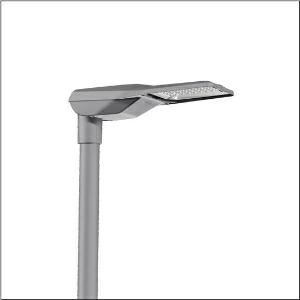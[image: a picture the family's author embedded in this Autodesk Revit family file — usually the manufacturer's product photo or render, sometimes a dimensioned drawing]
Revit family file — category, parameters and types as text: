
# Revit family: streetlight_sl_21_mini___st1_5a_5xe6p43a08hb_28db
name_source: partatom
category: Lighting Fixtures
units: mm (PartAtom-declared; Revit-internal decimal feet)

## family parameters
Cut with Voids When Loaded = No
Host = Face
Light Source = No
Part Type = Normal
Room Calculation Point = No
Round Connector Dimension = Use Diameter
Shared = No

## types (1)
- --- (1 x LED, 9260 lm, 66 W, 4000K)
    Apparent Load = 66 VA
    CIE Flux Codes = 22 53 95 100 100
    Color Rendering = 70
    Color Temperature = 4000K
    Default Elevation = 1800 mm
    Description = Streetlight SL 21 mini, mast luminaire, primary light control with lens, of PMMA, primary optical cover: cover, of toughened safety glass, transparent, light distribution: ST1.5a, light emission: direct distribution, primary light characteristic: asymmetric, installation type: post-top, side-entry, LED, 3G 1.5mm², High Power LED, rated luminous flux: 9.260lm, luminous efficacy: 140lm/W, light colour: 740, colour temperature: 4000K, control: overheat protection, constant luminous flux control, time-dependent luminous flux control, flexible luminous flux parameterisation, mains connection: 230..240V, AC, 50/60Hz, connection cable pre-assembled, cable length: 8,5m, wiring characteristics: H07RN-F, start of lifetime: 66W, end of service life: 69W, reduction: 30W, luminaire housing, of diecast aluminium, powder-coated, Siteco® metallic grey (DB 702S), corrosivity category C5 mid according to DIN EN ISO 12944, please order mast flange separately, inclination adjustable: 0°, 5°, 10°, 15°, sealing non-destructively replaceable, multi-level sealing system, length: 628mm, width: 235mm, height: 110mm, mast flange for spigot size: 42mm (side-entry): 5XC10008XM4, 60/48mm (side-entry/post-top): 5XC10108XM2, 76/60mm (side-entry/post-top): 5XC10108XM1, protection rating (complete): IP66, insulation class (complete): insulation class II (safety insulation), certification: CE, ENEC, ENEC+, VDE, impact resistance: IK09, permissible operating ambient temperature for outdoor applications: -40..+50°C, standard-compliant lighting for roads and squares, packaging unit: 1 piece

Light Distribution: ST1.5a
    Height = 110 mm
    Lamp = 1 x LED
    Lamp Light Flux = 9260 lm
    Lamp Power = 66 W
    Lamp count = 1
    Length = 625 mm
    Luminous efficacy = 140 lm/W
    Manufacturer = Siteco
    ModVariant = No
    Model = 5XE6P43A08HB
    Number of Poles = 1
    OnlyDefault = Yes
    Power Factor = 1
    Product Name = Streetlight SL 21 mini | ST1.5a
    Product group = mast luminaire | pylon top
    ProductGroupID = 6100
    Protection Class = Protection class II
    Protection Degree = IP 66
    RLX_Detail_Level = 1
    RLX_Emergency_Light_Flux = 0 lm
    RLX_Emergency_Type = 0
    RLX_Emergency_Type_DB = No
    RlxData = <blob elided: 96777 chars, md5=21d12b11>
    Socket = socket
    Standby Power = 0 W
    System Light Flux = 9260 lm
    System Power = 66 W
    Type Comments = factory setting: luminous flux: 100 % | Output Level: 100 % | 670 mA
    Type Image = l_1003519.jpg
    URL = http://relux.com
    VarID = @adj_126319
    Voltage = 0 V
    Weight = 0.00 kg
    Width = 234 mm

## geometry (parser evidence)
native form markers: Blend x4, Sweep x11
no freeform markers — native parametric forms only
